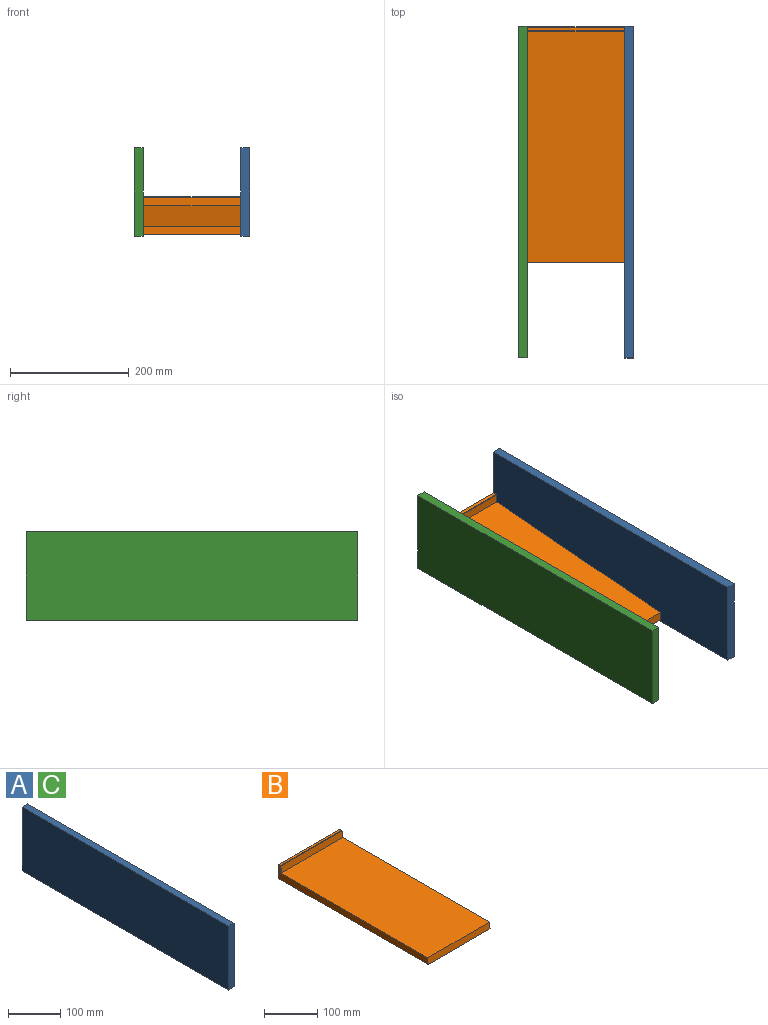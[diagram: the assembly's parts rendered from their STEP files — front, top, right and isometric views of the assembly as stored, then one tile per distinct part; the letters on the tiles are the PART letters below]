
ASSEMBLY  parts=3 mates=4
PART A: 6 faces, bbox 15x560x150 mm
  f0: plane 150x15mm, normal (0,-1,0), area 2250mm2, adj f1,f3,f4,f5
  f1: plane 560x15mm, normal (0,0,-1), area 8400mm2, adj f0,f2,f4,f5
  f2: plane 150x15mm, normal (0,1,0), area 2250mm2, adj f1,f3,f4,f5
  f3: plane 560x15mm, normal (0,0,1), area 8400mm2, adj f0,f2,f4,f5
  f4: plane 560x150mm, normal (1,0,0), area 84000mm2, adj f0,f1,f2,f3
  f5: plane 560x150mm, normal (-1,0,0), area 84000mm2, adj f0,f1,f2,f3
PART B: 22 faces, bbox 165x401.2x30.5 mm
  f0: plane 392.06x165mm, normal (0,0,1), area 64525.7mm2, adj f2,f3,f4,f13,f17,f19
  f1: plane 398.69x165mm, normal (0,0,-1), area 65782.5mm2, adj f2,f3,f4,f5,f14,f16
  f2: plane 400.22x29.47mm, normal (-1,0,0), area 6045.2mm2, adj f0,f1,f4,f16,f19,f21
  f3: plane 400.22x29.47mm, normal (1,0,0), area 5809.6mm2, adj f0,f1,f4,f7,f9,f11,f14,f17
  f4: plane 165x15mm, normal (0,-1,0.09), area 2484.5mm2, adj f0,f1,f2,f3
  f5: plane 163x28.89mm, normal (0,1,-0.09), area 4727mm2, adj f1,f14,f15,f16
  f6: cone r=0mm half-angle=59deg, axis (1,0,0), area 91.6mm2, adj f7
  f7: cylinder r=5mm len=20mm, axis (1,0,0), area 628.3mm2, adj f3,f6
  f8: cone r=0mm half-angle=59deg, axis (1,0,0), area 91.6mm2, adj f9
  f9: cylinder r=5mm len=20mm, axis (1,0,0), area 628.3mm2, adj f3,f8
  f10: cone r=0mm half-angle=59deg, axis (1,0,0), area 91.6mm2, adj f11
  f11: cylinder r=5mm len=20mm, axis (1,0,0), area 628.3mm2, adj f3,f10
  f12: plane 163x5.58mm, normal (0,0.09,1), area 912.8mm2, adj f15,f18,f20,f21
  f13: plane 163x14.55mm, normal (0,-1,0.09), area 2381mm2, adj f0,f17,f18,f19
  f14: plane 29.43x3.53mm, normal (0.71,0.7,-0.06), area 41.4mm2, adj f1,f3,f5,f15,f20
  f15: plane 164x1.08mm, normal (0,0.77,0.64), area 231.2mm2, adj f5,f12,f14,f16,f20,f21
  f16: plane 29.43x3.53mm, normal (-0.71,0.7,-0.06), area 41.4mm2, adj f1,f2,f5,f15,f21
  f17: plane 15.01x2.27mm, normal (0.71,-0.7,0.06), area 20.9mm2, adj f0,f3,f13,f18,f20
  f18: plane 164x1.08mm, normal (0,-0.64,0.77), area 231.2mm2, adj f12,f13,f17,f19,f20,f21
  f19: plane 15.01x2.27mm, normal (-0.71,-0.7,0.06), area 20.9mm2, adj f0,f2,f13,f18,f21
  f20: plane 6.58x1.48mm, normal (0.71,0.06,0.7), area 8.6mm2, adj f3,f12,f14,f15,f17,f18
  f21: plane 6.58x1.48mm, normal (-0.71,0.06,0.7), area 8.6mm2, adj f2,f12,f15,f16,f18,f19
PART C: same geometry as A
PLACE A t=(-93,0,0)mm
PLACE B rot(axis=(1,0,0),5deg) t=(-258,160.15,17.43)mm
PLACE C t=(-273,0,0)mm
MATE planar B.f2 <-> C.f4  axis (-1,0,0) through (-258,362.13,27.77)mm
MATE planar C.f2 <-> A.f2  axis (0,1,0) through (-265.5,560,75)mm
MATE planar A.f5 <-> B.f8  axis (-1,0,0) through (-93,280,75)mm
MATE planar A.f2 <-> C.f2  axis (0,1,0) through (-85.5,560,75)mm
